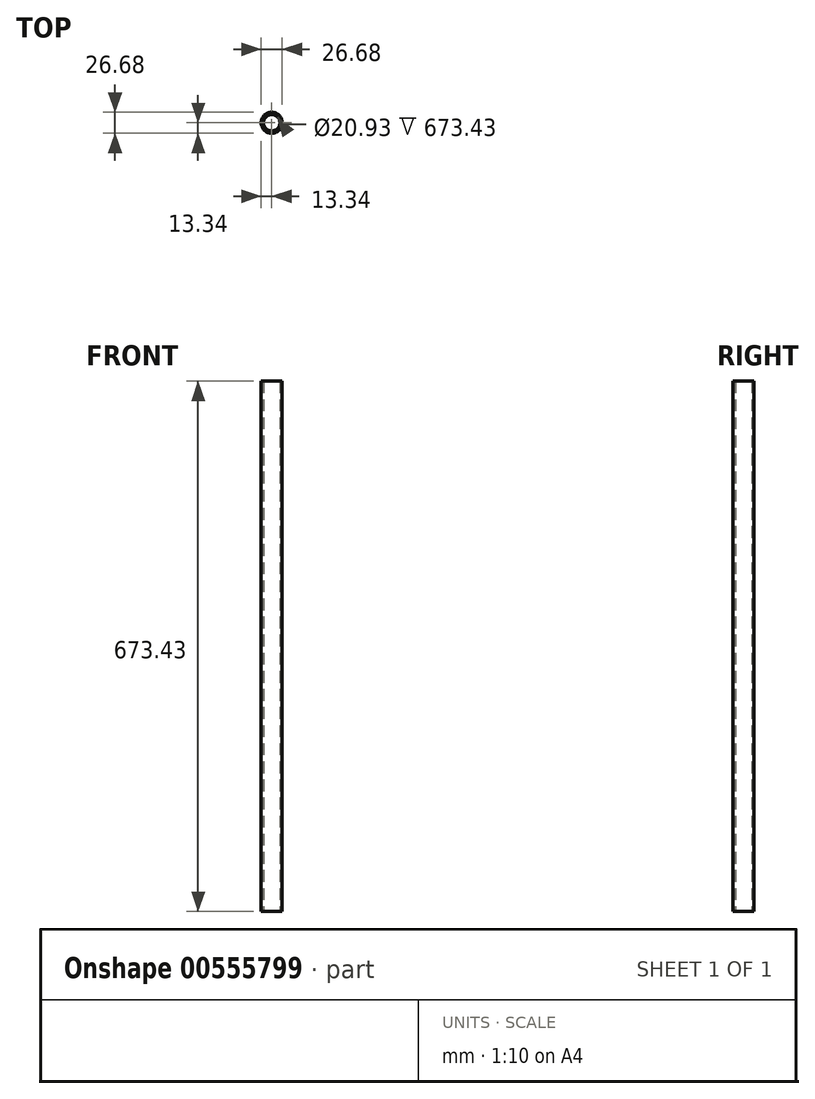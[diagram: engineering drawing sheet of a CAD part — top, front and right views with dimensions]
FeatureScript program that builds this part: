
annotation { "Feature Type Name" : "Feature", "Feature Type Description" : "" }
export const myFeature = defineFeature(function(context is Context, id is Id, definition is map)
    precondition{}
    {
        {
            var Q0;
            Q0=qCreatedBy(makeId("Top.planeOp"),FACE);
            var sketch = newSketch(context, id + "F0", { "sketchPlane" : qUnion([Q0])});
            skCircle(sketch, "E0", {"center": v(0, 0) * mm, "radius": 13.33 * mm});
            skCircle(sketch, "E1", {"center": v(0, 0) * mm, "radius": 10.46 * mm});
            skSolve(sketch);
        }
        {
            var Q0;
            Q0=qSketchRegion(id+"F0",true);
            extrude(context, id + "F1", {"entities" : qUnion([Q0]), "depth" : 673.43 * mm, "offsetDistance" : 25.4 * mm});
        }
    });
